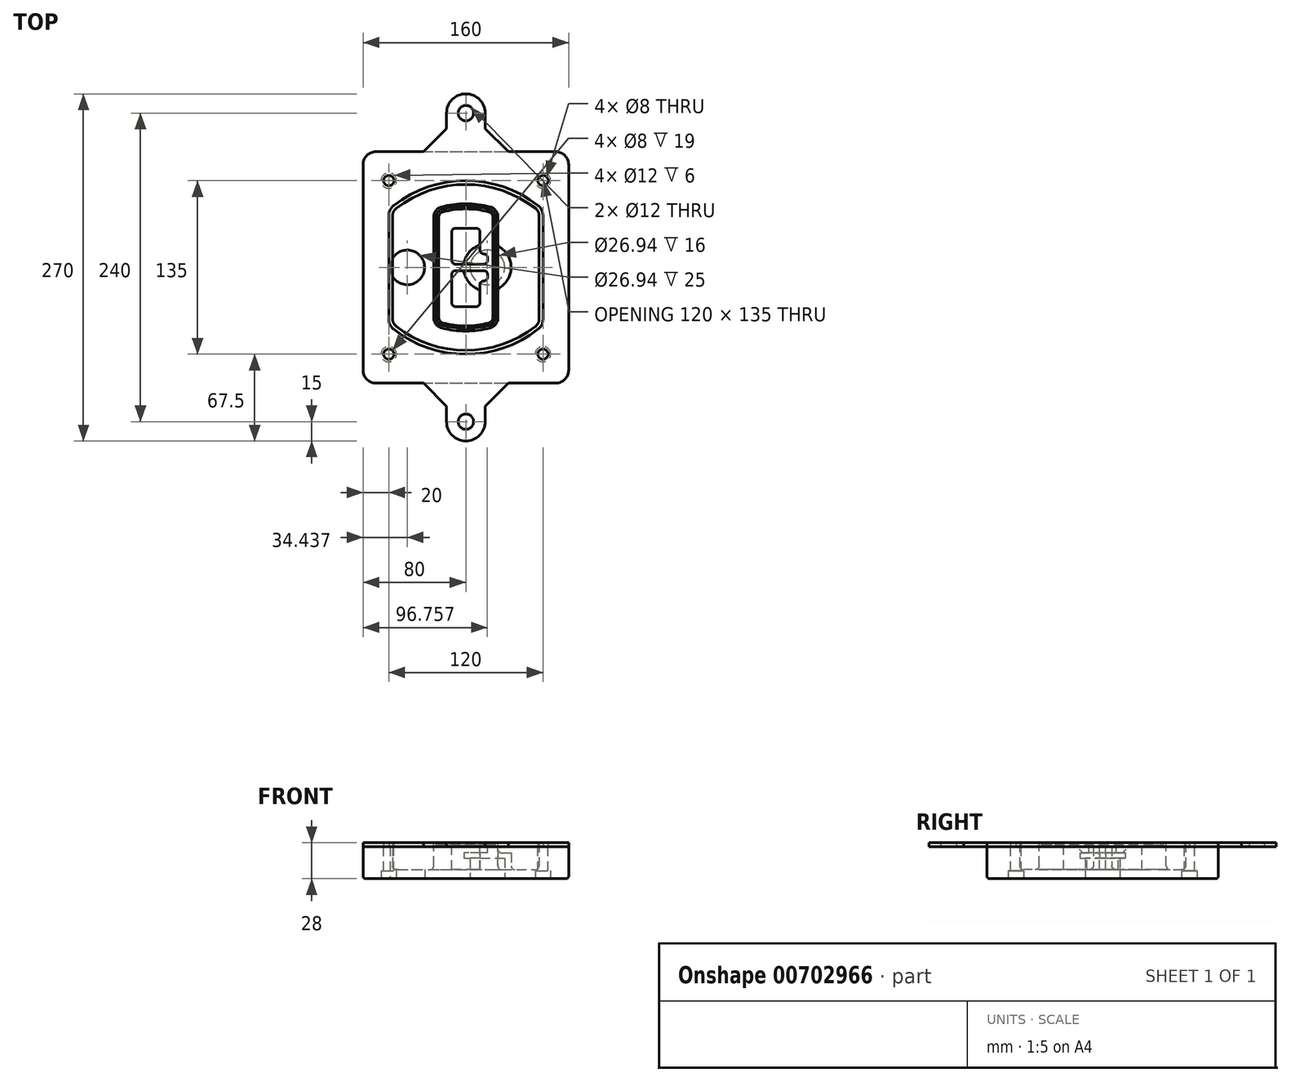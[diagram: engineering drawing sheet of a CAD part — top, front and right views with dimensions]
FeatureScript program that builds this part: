
annotation { "Feature Type Name" : "Feature", "Feature Type Description" : "" }
export const myFeature = defineFeature(function(context is Context, id is Id, definition is map)
    precondition{}
    {
        {
            var Q0;
            Q0=qCreatedBy(makeId("Top.planeOp"),FACE);
            var sketch = newSketch(context, id + "F0", { "sketchPlane" : qUnion([Q0])});
            skPoint(sketch, "E0.rect.middle", {"position": v(0, 0) * mm});
            skLineSegment(sketch, "E1.bottom", {"start": v(-70, -90) * mm, "end": v(70, -90) * mm});
            skLineSegment(sketch, "E1.top", {"start": v(-70, 90) * mm, "end": v(70, 90) * mm});
            skLineSegment(sketch, "E1.left", {"start": v(-80, -80) * mm, "end": v(-80, 80) * mm});
            skLineSegment(sketch, "E1.right", {"start": v(80, -80) * mm, "end": v(80, 80) * mm});
            skLineSegment(sketch, "E2", {"start": v(-80, 90) * mm, "end": v(80, -90) * mm, "construction": true});
            skLineSegment(sketch, "E3", {"start": v(80, 90) * mm, "end": v(-80, -90) * mm, "construction": true});
            skCircle(sketch, "E4", {"center": v(-60, 67.5) * mm, "radius": 4 * mm});
            skCircle(sketch, "E5", {"center": v(60, 67.5) * mm, "radius": 4 * mm});
            skCircle(sketch, "E6", {"center": v(60, -67.5) * mm, "radius": 4 * mm});
            skCircle(sketch, "E7", {"center": v(-60, -67.5) * mm, "radius": 4 * mm});
            skLineSegment(sketch, "E8", {"start": v(-60, 67.5) * mm, "end": v(60, 67.5) * mm, "construction": true});
            skLineSegment(sketch, "E9", {"start": v(60, 67.5) * mm, "end": v(60, -67.5) * mm, "construction": true});
            skLineSegment(sketch, "E10", {"start": v(60, -67.5) * mm, "end": v(-60, -67.5) * mm, "construction": true});
            skLineSegment(sketch, "E11", {"start": v(-60, -67.5) * mm, "end": v(-60, 67.5) * mm, "construction": true});
            skLineSegment(sketch, "E12", {"start": v(-60, 40.3) * mm, "end": v(-60, -40.3) * mm});
            skLineSegment(sketch, "E13", {"start": v(60, 40.3) * mm, "end": v(60, -40.3) * mm});
            skArc(sketch, "E14", {"start": v(56.15, 48.18) * mm, "mid": v(0, 67.5) * mm, "end": v(-56.15, 48.18) * mm});
            skArc(sketch, "E15", {"start": v(-56.15, -48.18) * mm, "mid": v(0, -67.5) * mm, "end": v(56.15, -48.18) * mm});
            skLineSegment(sketch, "E16", {"start": v(-60, 0) * mm, "end": v(60, 0) * mm, "construction": true});
            skPoint(sketch, "E17.visualSharp", {"position": v(-60, -45) * mm});
            skArc(sketch, "E17.filletArc", {"start": v(-60, -40.3) * mm, "mid": v(-58.99, -44.68) * mm, "end": v(-56.15, -48.18) * mm});
            skPoint(sketch, "E18.visualSharp", {"position": v(-60, 45) * mm});
            skArc(sketch, "E18.filletArc", {"start": v(-56.15, 48.18) * mm, "mid": v(-58.99, 44.68) * mm, "end": v(-60, 40.3) * mm});
            skPoint(sketch, "E19.visualSharp", {"position": v(60, 45) * mm});
            skArc(sketch, "E19.filletArc", {"start": v(60, 40.3) * mm, "mid": v(58.99, 44.68) * mm, "end": v(56.15, 48.18) * mm});
            skPoint(sketch, "E20.visualSharp", {"position": v(60, -45) * mm});
            skArc(sketch, "E20.filletArc", {"start": v(56.15, -48.18) * mm, "mid": v(58.99, -44.68) * mm, "end": v(60, -40.3) * mm});
            skPoint(sketch, "E21.visualSharp", {"position": v(-80, 90) * mm});
            skArc(sketch, "E21.filletArc", {"start": v(-70, 90) * mm, "mid": v(-77.07, 87.07) * mm, "end": v(-80, 80) * mm});
            skPoint(sketch, "E22.visualSharp", {"position": v(80, 90) * mm});
            skArc(sketch, "E22.filletArc", {"start": v(80, 80) * mm, "mid": v(77.07, 87.07) * mm, "end": v(70, 90) * mm});
            skPoint(sketch, "E23.visualSharp", {"position": v(80, -90) * mm});
            skArc(sketch, "E23.filletArc", {"start": v(70, -90) * mm, "mid": v(77.07, -87.07) * mm, "end": v(80, -80) * mm});
            skPoint(sketch, "E24.visualSharp", {"position": v(-80, -90) * mm});
            skArc(sketch, "E24.filletArc", {"start": v(-80, -80) * mm, "mid": v(-77.07, -87.07) * mm, "end": v(-70, -90) * mm});
            skArc(sketch, "E25.0", {"start": v(57, 40.3) * mm, "mid": v(56.3, 43.36) * mm, "end": v(54.3, 45.81) * mm});
            skLineSegment(sketch, "E25.1", {"start": v(57, 40.3) * mm, "end": v(57, -40.3) * mm});
            skArc(sketch, "E25.2", {"start": v(54.3, -45.81) * mm, "mid": v(56.3, -43.36) * mm, "end": v(57, -40.3) * mm});
            skArc(sketch, "E25.3", {"start": v(-54.3, -45.81) * mm, "mid": v(0, -64.5) * mm, "end": v(54.3, -45.81) * mm});
            skArc(sketch, "E25.4", {"start": v(-57, -40.3) * mm, "mid": v(-56.3, -43.36) * mm, "end": v(-54.3, -45.81) * mm});
            skArc(sketch, "E25.5", {"start": v(54.3, 45.81) * mm, "mid": v(0, 64.5) * mm, "end": v(-54.3, 45.81) * mm});
            skLineSegment(sketch, "E25.6", {"start": v(-57, 40.3) * mm, "end": v(-57, -40.3) * mm});
            skArc(sketch, "E25.7", {"start": v(-54.3, 45.81) * mm, "mid": v(-56.3, 43.36) * mm, "end": v(-57, 40.3) * mm});
            skArc(sketch, "E26.0", {"start": v(-58.62, 51.33) * mm, "mid": v(-62.58, 46.43) * mm, "end": v(-64, 40.3) * mm});
            skArc(sketch, "E26.1", {"start": v(58.62, 51.33) * mm, "mid": v(0, 71.5) * mm, "end": v(-58.62, 51.33) * mm});
            skArc(sketch, "E26.2", {"start": v(64, 40.3) * mm, "mid": v(62.58, 46.43) * mm, "end": v(58.62, 51.33) * mm});
            skLineSegment(sketch, "E26.3", {"start": v(64, 40.3) * mm, "end": v(64, -40.3) * mm});
            skArc(sketch, "E26.4", {"start": v(58.62, -51.33) * mm, "mid": v(62.58, -46.43) * mm, "end": v(64, -40.3) * mm});
            skLineSegment(sketch, "E26.5", {"start": v(-64, 40.3) * mm, "end": v(-64, -40.3) * mm});
            skArc(sketch, "E26.6", {"start": v(-58.62, -51.33) * mm, "mid": v(0, -71.5) * mm, "end": v(58.62, -51.33) * mm});
            skArc(sketch, "E26.7", {"start": v(-64, -40.3) * mm, "mid": v(-62.58, -46.43) * mm, "end": v(-58.62, -51.33) * mm});
            skSolve(sketch);
        }
        {
            var Q0;
            Q0=makeQuery(id+"F0.imprint","IMPRINT",FACE,{"disambiguationData":[TD([[makeQuery(id+"F0.imprint","IMPRINT",EDGE,{"derivedFrom":sQuery(id+"F0.wireOp",EDGE,"E1.bottom")}),1.0]])]});
            var Q1;
            Q1=makeQuery(id+"F0.imprint","IMPRINT",FACE,{"disambiguationData":[TD([[makeQuery(id+"F0.imprint","IMPRINT",EDGE,{"derivedFrom":sQuery(id+"F0.wireOp",EDGE,"E12")}),1.0]])]});
            var Q2;
            Q2=makeQuery(id+"F0.imprint","IMPRINT",FACE,{"disambiguationData":[TD([[makeQuery(id+"F0.imprint","IMPRINT",EDGE,{"derivedFrom":sQuery(id+"F0.wireOp",EDGE,"E25.0")}),1.0]])]});
            var Q3;
            Q3=makeQuery(id+"F0.imprint","IMPRINT",FACE,{"disambiguationData":[TD([[makeQuery(id+"F0.imprint","IMPRINT",EDGE,{"derivedFrom":sQuery(id+"F0.wireOp",EDGE,"E12")}),-1.0]])]});
            extrude(context, id + "F1", {"entities" : qUnion([Q0, Q1, Q2, Q3]), "oppositeDirection" : true, "depth" : 25 * mm});
        }
        {
            var Q0;
            Q0=makeQuery(id+"F0.imprint","IMPRINT",FACE,{"disambiguationData":[TD([[makeQuery(id+"F0.imprint","IMPRINT",EDGE,{"derivedFrom":sQuery(id+"F0.wireOp",EDGE,"E12")}),1.0]])]});
            extrude(context, id + "F2", {"entities" : qUnion([Q0]), "operationType" : NewBodyOperationType.ADD, "depth" : 3 * mm});
        }
        {
            var Q0;
            Q0=makeQuery(id+"F0.imprint","IMPRINT",FACE,{"disambiguationData":[TD([[makeQuery(id+"F0.imprint","IMPRINT",EDGE,{"derivedFrom":sQuery(id+"F0.wireOp",EDGE,"E25.0")}),1.0]])]});
            extrude(context, id + "F3", {"entities" : qUnion([Q0]), "operationType" : NewBodyOperationType.REMOVE, "oppositeDirection" : true, "depth" : 18 * mm});
        }
        {
            var Q0;
            Q0=makeQuery(id+"F2.opExtrude","CAP_FACE",FACE,{"disambiguationData":[OSD([sQuery(id+"F0.wireOp",EDGE,"E12"),sQuery(id+"F0.wireOp",EDGE,"E13"),sQuery(id+"F0.wireOp",EDGE,"E14"),sQuery(id+"F0.wireOp",EDGE,"E15"),sQuery(id+"F0.wireOp",EDGE,"E17.filletArc"),sQuery(id+"F0.wireOp",EDGE,"E18.filletArc"),sQuery(id+"F0.wireOp",EDGE,"E19.filletArc"),sQuery(id+"F0.wireOp",EDGE,"E20.filletArc"),sQuery(id+"F0.wireOp",EDGE,"E25.0"),sQuery(id+"F0.wireOp",EDGE,"E25.1"),sQuery(id+"F0.wireOp",EDGE,"E25.2"),sQuery(id+"F0.wireOp",EDGE,"E25.3"),sQuery(id+"F0.wireOp",EDGE,"E25.4"),sQuery(id+"F0.wireOp",EDGE,"E25.5"),sQuery(id+"F0.wireOp",EDGE,"E25.6"),sQuery(id+"F0.wireOp",EDGE,"E25.7")])],"isStart":false});
            var sketch = newSketch(context, id + "F4", { "sketchPlane" : qUnion([Q0])});
            skArc(sketch, "E27.0", {"start": v(-19.08, -46.97) * mm, "mid": v(0, -49.5) * mm, "end": v(19.08, -46.97) * mm});
            skArc(sketch, "E28.0", {"start": v(19.08, 46.97) * mm, "mid": v(0, 49.5) * mm, "end": v(-19.08, 46.97) * mm});
            skLineSegment(sketch, "E29", {"start": v(-25, 39.25) * mm, "end": v(-25, -39.25) * mm});
            skLineSegment(sketch, "E30", {"start": v(25, 39.25) * mm, "end": v(25, -39.25) * mm});
            skLineSegment(sketch, "E31", {"start": v(-25, 45.1) * mm, "end": v(25, 45.1) * mm, "construction": true});
            skLineSegment(sketch, "E32", {"start": v(-25, -45.1) * mm, "end": v(25, -45.1) * mm, "construction": true});
            skPoint(sketch, "E33.visualSharp", {"position": v(-25, 45.1) * mm});
            skArc(sketch, "E33.filletArc", {"start": v(-19.08, 46.97) * mm, "mid": v(-23.35, 44.11) * mm, "end": v(-25, 39.25) * mm});
            skPoint(sketch, "E34.visualSharp", {"position": v(25, 45.1) * mm});
            skArc(sketch, "E34.filletArc", {"start": v(25, 39.25) * mm, "mid": v(23.35, 44.11) * mm, "end": v(19.08, 46.97) * mm});
            skPoint(sketch, "E35.visualSharp", {"position": v(25, -45.1) * mm});
            skArc(sketch, "E35.filletArc", {"start": v(19.08, -46.97) * mm, "mid": v(23.35, -44.11) * mm, "end": v(25, -39.25) * mm});
            skPoint(sketch, "E36.visualSharp", {"position": v(-25, -45.1) * mm});
            skArc(sketch, "E36.filletArc", {"start": v(-25, -39.25) * mm, "mid": v(-23.35, -44.11) * mm, "end": v(-19.08, -46.97) * mm});
            skArc(sketch, "E37.0", {"start": v(54.3, 45.81) * mm, "mid": v(0, 64.5) * mm, "end": v(-54.3, 45.81) * mm});
            skArc(sketch, "E37.1", {"start": v(-54.3, 45.81) * mm, "mid": v(-56.3, 43.36) * mm, "end": v(-57, 40.3) * mm});
            skLineSegment(sketch, "E37.2", {"start": v(-57, 40.3) * mm, "end": v(-57, -40.3) * mm});
            skArc(sketch, "E37.3", {"start": v(-57, -40.3) * mm, "mid": v(-56.3, -43.36) * mm, "end": v(-54.3, -45.81) * mm});
            skArc(sketch, "E37.4", {"start": v(-54.3, -45.81) * mm, "mid": v(0, -64.5) * mm, "end": v(54.3, -45.81) * mm});
            skArc(sketch, "E37.5", {"start": v(54.3, -45.81) * mm, "mid": v(56.3, -43.36) * mm, "end": v(57, -40.3) * mm});
            skLineSegment(sketch, "E37.6", {"start": v(57, 40.3) * mm, "end": v(57, -40.3) * mm});
            skArc(sketch, "E37.7", {"start": v(57, 40.3) * mm, "mid": v(56.3, 43.36) * mm, "end": v(54.3, 45.81) * mm});
            skLineSegment(sketch, "E38.0", {"start": v(23, 39.25) * mm, "end": v(23, -39.25) * mm});
            skArc(sketch, "E38.1", {"start": v(18.56, -45.04) * mm, "mid": v(21.76, -42.9) * mm, "end": v(23, -39.25) * mm});
            skArc(sketch, "E38.2", {"start": v(-18.56, -45.04) * mm, "mid": v(0, -47.5) * mm, "end": v(18.56, -45.04) * mm});
            skArc(sketch, "E38.3", {"start": v(-23, -39.25) * mm, "mid": v(-21.76, -42.9) * mm, "end": v(-18.56, -45.04) * mm});
            skLineSegment(sketch, "E38.4", {"start": v(-23, 39.25) * mm, "end": v(-23, -39.25) * mm});
            skArc(sketch, "E38.5", {"start": v(23, 39.25) * mm, "mid": v(21.76, 42.9) * mm, "end": v(18.56, 45.04) * mm});
            skArc(sketch, "E38.6", {"start": v(-18.56, 45.04) * mm, "mid": v(-21.76, 42.9) * mm, "end": v(-23, 39.25) * mm});
            skArc(sketch, "E38.7", {"start": v(18.56, 45.04) * mm, "mid": v(0, 47.5) * mm, "end": v(-18.56, 45.04) * mm});
            skArc(sketch, "E39.0", {"start": v(21, 39.25) * mm, "mid": v(20.18, 41.68) * mm, "end": v(18.04, 43.1) * mm});
            skLineSegment(sketch, "E39.1", {"start": v(21, 39.25) * mm, "end": v(21, -39.25) * mm});
            skArc(sketch, "E39.2", {"start": v(18.04, -43.1) * mm, "mid": v(20.18, -41.68) * mm, "end": v(21, -39.25) * mm});
            skArc(sketch, "E39.3", {"start": v(-18.04, -43.1) * mm, "mid": v(0, -45.5) * mm, "end": v(18.04, -43.1) * mm});
            skArc(sketch, "E39.4", {"start": v(-21, -39.25) * mm, "mid": v(-20.18, -41.68) * mm, "end": v(-18.04, -43.1) * mm});
            skArc(sketch, "E39.5", {"start": v(18.04, 43.1) * mm, "mid": v(0, 45.5) * mm, "end": v(-18.04, 43.1) * mm});
            skLineSegment(sketch, "E39.6", {"start": v(-21, 39.25) * mm, "end": v(-21, -39.25) * mm});
            skArc(sketch, "E39.7", {"start": v(-18.04, 43.1) * mm, "mid": v(-20.18, 41.68) * mm, "end": v(-21, 39.25) * mm});
            skLineSegment(sketch, "E40", {"start": v(-25, 0) * mm, "end": v(25, 0) * mm, "construction": true});
            skLineSegment(sketch, "E41", {"start": v(-11, 5.5) * mm, "end": v(-11, 27.5) * mm});
            skLineSegment(sketch, "E42", {"start": v(-8, 30.5) * mm, "end": v(8, 30.5) * mm});
            skLineSegment(sketch, "E43", {"start": v(11, 27.5) * mm, "end": v(11, 13.5) * mm});
            skLineSegment(sketch, "E44", {"start": v(14, 10.5) * mm, "end": v(14, 10.5) * mm});
            skLineSegment(sketch, "E45", {"start": v(17, 7.5) * mm, "end": v(17, 5.5) * mm});
            skLineSegment(sketch, "E46", {"start": v(14, 2.5) * mm, "end": v(-8, 2.5) * mm});
            skPoint(sketch, "E47.visualSharp", {"position": v(-11, 30.5) * mm});
            skArc(sketch, "E47.filletArc", {"start": v(-8, 30.5) * mm, "mid": v(-10.12, 29.62) * mm, "end": v(-11, 27.5) * mm});
            skPoint(sketch, "E48.visualSharp", {"position": v(11, 30.5) * mm});
            skArc(sketch, "E48.filletArc", {"start": v(11, 27.5) * mm, "mid": v(10.12, 29.62) * mm, "end": v(8, 30.5) * mm});
            skPoint(sketch, "E49.visualSharp", {"position": v(11, 10.5) * mm});
            skArc(sketch, "E49.filletArc", {"start": v(11, 13.5) * mm, "mid": v(11.88, 11.38) * mm, "end": v(14, 10.5) * mm});
            skPoint(sketch, "E50.visualSharp", {"position": v(17, 10.5) * mm});
            skArc(sketch, "E50.filletArc", {"start": v(17, 7.5) * mm, "mid": v(16.12, 9.62) * mm, "end": v(14, 10.5) * mm});
            skPoint(sketch, "E51.visualSharp", {"position": v(17, 2.5) * mm});
            skArc(sketch, "E51.filletArc", {"start": v(14, 2.5) * mm, "mid": v(16.12, 3.38) * mm, "end": v(17, 5.5) * mm});
            skPoint(sketch, "E52.visualSharp", {"position": v(-11, 2.5) * mm});
            skArc(sketch, "E52.filletArc", {"start": v(-11, 5.5) * mm, "mid": v(-10.12, 3.38) * mm, "end": v(-8, 2.5) * mm});
            skLineSegment(sketch, "E53.0.MirrorCS", {"start": v(14, -2.5) * mm, "end": v(-8, -2.5) * mm});
            skArc(sketch, "E54.0.MirrorCS", {"start": v(-11, -5.5) * mm, "mid": v(-10.12, -3.38) * mm, "end": v(-8, -2.5) * mm});
            skLineSegment(sketch, "E55.0.MirrorCS", {"start": v(-11, -5.5) * mm, "end": v(-11, -27.5) * mm});
            skArc(sketch, "E56.0.MirrorCS", {"start": v(-8, -30.5) * mm, "mid": v(-10.12, -29.62) * mm, "end": v(-11, -27.5) * mm});
            skLineSegment(sketch, "E57.0.MirrorCS", {"start": v(-8, -30.5) * mm, "end": v(8, -30.5) * mm});
            skArc(sketch, "E58.0.MirrorCS", {"start": v(11, -27.5) * mm, "mid": v(10.12, -29.62) * mm, "end": v(8, -30.5) * mm});
            skLineSegment(sketch, "E59.0.MirrorCS", {"start": v(11, -27.5) * mm, "end": v(11, -13.5) * mm});
            skArc(sketch, "E60.0.MirrorCS", {"start": v(11, -13.5) * mm, "mid": v(11.88, -11.38) * mm, "end": v(14, -10.5) * mm});
            skArc(sketch, "E61.0.MirrorCS", {"start": v(17, -7.5) * mm, "mid": v(16.12, -9.62) * mm, "end": v(14, -10.5) * mm});
            skLineSegment(sketch, "E62.0.MirrorCS", {"start": v(17, -7.5) * mm, "end": v(17, -5.5) * mm});
            skArc(sketch, "E63.0.MirrorCS", {"start": v(14, -2.5) * mm, "mid": v(16.12, -3.38) * mm, "end": v(17, -5.5) * mm});
            skSolve(sketch);
        }
        {
            var Q0;
            Q0=makeQuery(id+"F4.imprint","IMPRINT",FACE,{"disambiguationData":[TD([[makeQuery(id+"F4.imprint","IMPRINT",EDGE,{"derivedFrom":sQuery(id+"F4.wireOp",EDGE,"E27.0")}),1.0]])]});
            var Q1;
            Q1=makeQuery(id+"F4.imprint","IMPRINT",FACE,{"disambiguationData":[TD([[makeQuery(id+"F4.imprint","IMPRINT",EDGE,{"derivedFrom":sQuery(id+"F4.wireOp",EDGE,"E38.0")}),-1.0]])]});
            var Q2;
            Q2=makeQuery(id+"F4.imprint","IMPRINT",FACE,{"disambiguationData":[TD([[makeQuery(id+"F4.imprint","IMPRINT",EDGE,{"derivedFrom":sQuery(id+"F4.wireOp",EDGE,"E39.0")}),1.0]])]});
            extrude(context, id + "F5", {"entities" : qUnion([Q0, Q1, Q2]), "operationType" : NewBodyOperationType.ADD, "endBound" : BoundingType.UP_TO_NEXT, "oppositeDirection" : true, "depth" : 25 * mm});
        }
        {
            var Q0;
            Q0=makeQuery(id+"F4.imprint","IMPRINT",FACE,{"disambiguationData":[TD([[makeQuery(id+"F4.imprint","IMPRINT",EDGE,{"derivedFrom":sQuery(id+"F4.wireOp",EDGE,"E38.0")}),-1.0]])]});
            extrude(context, id + "F6", {"entities" : qUnion([Q0]), "operationType" : NewBodyOperationType.REMOVE, "oppositeDirection" : true, "depth" : 2 * mm});
        }
        {
            var Q0;
            Q0=makeQuery(id+"F1.opExtrude","CAP_FACE",FACE,{"disambiguationData":[OSD([sQuery(id+"F0.wireOp",EDGE,"E1.bottom"),sQuery(id+"F0.wireOp",EDGE,"E1.top"),sQuery(id+"F0.wireOp",EDGE,"E1.left"),sQuery(id+"F0.wireOp",EDGE,"E1.right"),sQuery(id+"F0.wireOp",EDGE,"E4"),sQuery(id+"F0.wireOp",EDGE,"E5"),sQuery(id+"F0.wireOp",EDGE,"E6"),sQuery(id+"F0.wireOp",EDGE,"E7"),sQuery(id+"F0.wireOp",EDGE,"E21.filletArc"),sQuery(id+"F0.wireOp",EDGE,"E22.filletArc"),sQuery(id+"F0.wireOp",EDGE,"E23.filletArc"),sQuery(id+"F0.wireOp",EDGE,"E24.filletArc")])],"isStart":false});
            var sketch = newSketch(context, id + "F7", { "sketchPlane" : qUnion([Q0])});
            skCircle(sketch, "E64", {"center": v(16.76, 0) * mm, "radius": 13.47 * mm});
            skCircle(sketch, "E65", {"center": v(-45.56, 0) * mm, "radius": 13.47 * mm});
            skLineSegment(sketch, "E66", {"start": v(80, 0) * mm, "end": v(-80, 0) * mm});
            skCircle(sketch, "E67", {"center": v(16.76, 0) * mm, "radius": 18.47 * mm});
            skCircle(sketch, "E68", {"center": v(60, -67.5) * mm, "radius": 6 * mm});
            skCircle(sketch, "E69", {"center": v(-60, -67.5) * mm, "radius": 6 * mm});
            skCircle(sketch, "E70", {"center": v(-60, 67.5) * mm, "radius": 6 * mm});
            skCircle(sketch, "E71", {"center": v(60, 67.5) * mm, "radius": 6 * mm});
            skSolve(sketch);
        }
        {
            var Q0;
            {var subQ1=sQuery(id+"F7.wireOp",EDGE,"E66");var subQ4=sQuery(id+"F7.wireOp",EDGE,"E64");var subQ6=makeQuery(id+"F7.imprint","INTERSECT",VERTEX,{"disambiguationData":[OD(0.0)],"derivedFrom":[subQ4,subQ1]});Q0=makeQuery(id+"F7.imprint","IMPRINT",FACE,{"disambiguationData":[TD([[makeQuery(id+"F7.imprint","IMPRINT",EDGE,{"disambiguationData":[TD([[subQ6,-1.0]])],"derivedFrom":subQ4}),-1.0]])]});}
            var Q1;
            {var subQ0=sQuery(id+"F7.wireOp",EDGE,"E66");var subQ1=sQuery(id+"F7.wireOp",EDGE,"E64");var subQ3=makeQuery(id+"F7.imprint","INTERSECT",VERTEX,{"disambiguationData":[OD(0.0)],"derivedFrom":[subQ1,subQ0]});Q1=makeQuery(id+"F7.imprint","IMPRINT",FACE,{"disambiguationData":[TD([[makeQuery(id+"F7.imprint","IMPRINT",EDGE,{"disambiguationData":[TD([[subQ3,-1.0]])],"derivedFrom":subQ1}),1.0]])]});}
            var Q2;
            {var subQ0=sQuery(id+"F7.wireOp",EDGE,"E66");var subQ1=sQuery(id+"F7.wireOp",EDGE,"E64");var subQ3=makeQuery(id+"F7.imprint","INTERSECT",VERTEX,{"disambiguationData":[OD(0.0)],"derivedFrom":[subQ1,subQ0]});Q2=makeQuery(id+"F7.imprint","IMPRINT",FACE,{"disambiguationData":[TD([[makeQuery(id+"F7.imprint","IMPRINT",EDGE,{"disambiguationData":[TD([[subQ3,1.0]])],"derivedFrom":subQ1}),1.0]])]});}
            var Q3;
            {var subQ1=sQuery(id+"F7.wireOp",EDGE,"E66");var subQ4=sQuery(id+"F7.wireOp",EDGE,"E64");var subQ6=makeQuery(id+"F7.imprint","INTERSECT",VERTEX,{"disambiguationData":[OD(0.0)],"derivedFrom":[subQ4,subQ1]});Q3=makeQuery(id+"F7.imprint","IMPRINT",FACE,{"disambiguationData":[TD([[makeQuery(id+"F7.imprint","IMPRINT",EDGE,{"disambiguationData":[TD([[subQ6,1.0]])],"derivedFrom":subQ4}),-1.0]])]});}
            extrude(context, id + "F8", {"entities" : qUnion([Q0, Q1, Q2, Q3]), "operationType" : NewBodyOperationType.ADD, "oppositeDirection" : true, "depth" : 20 * mm});
        }
        {
            var Q0;
            {var subQ0=sQuery(id+"F7.wireOp",EDGE,"E66");var subQ1=sQuery(id+"F7.wireOp",EDGE,"E64");var subQ3=makeQuery(id+"F7.imprint","INTERSECT",VERTEX,{"disambiguationData":[OD(0.0)],"derivedFrom":[subQ1,subQ0]});Q0=makeQuery(id+"F7.imprint","IMPRINT",FACE,{"disambiguationData":[TD([[makeQuery(id+"F7.imprint","IMPRINT",EDGE,{"disambiguationData":[TD([[subQ3,-1.0]])],"derivedFrom":subQ1}),1.0]])]});}
            var Q1;
            {var subQ0=sQuery(id+"F7.wireOp",EDGE,"E66");var subQ1=sQuery(id+"F7.wireOp",EDGE,"E64");var subQ3=makeQuery(id+"F7.imprint","INTERSECT",VERTEX,{"disambiguationData":[OD(0.0)],"derivedFrom":[subQ1,subQ0]});Q1=makeQuery(id+"F7.imprint","IMPRINT",FACE,{"disambiguationData":[TD([[makeQuery(id+"F7.imprint","IMPRINT",EDGE,{"disambiguationData":[TD([[subQ3,1.0]])],"derivedFrom":subQ1}),1.0]])]});}
            extrude(context, id + "F9", {"entities" : qUnion([Q0, Q1]), "operationType" : NewBodyOperationType.REMOVE, "oppositeDirection" : true, "depth" : 16 * mm});
        }
        {
            var Q0;
            {var subQ0=sQuery(id+"F7.wireOp",EDGE,"E66");var subQ1=sQuery(id+"F7.wireOp",EDGE,"E65");var subQ3=makeQuery(id+"F7.imprint","INTERSECT",VERTEX,{"disambiguationData":[OD(0.0)],"derivedFrom":[subQ1,subQ0]});Q0=makeQuery(id+"F7.imprint","IMPRINT",FACE,{"disambiguationData":[TD([[makeQuery(id+"F7.imprint","IMPRINT",EDGE,{"disambiguationData":[TD([[subQ3,-1.0]])],"derivedFrom":subQ1}),1.0]])]});}
            var Q1;
            {var subQ0=sQuery(id+"F7.wireOp",EDGE,"E66");var subQ1=sQuery(id+"F7.wireOp",EDGE,"E65");var subQ3=makeQuery(id+"F7.imprint","INTERSECT",VERTEX,{"disambiguationData":[OD(0.0)],"derivedFrom":[subQ1,subQ0]});Q1=makeQuery(id+"F7.imprint","IMPRINT",FACE,{"disambiguationData":[TD([[makeQuery(id+"F7.imprint","IMPRINT",EDGE,{"disambiguationData":[TD([[subQ3,1.0]])],"derivedFrom":subQ1}),1.0]])]});}
            extrude(context, id + "F10", {"entities" : qUnion([Q0, Q1]), "operationType" : NewBodyOperationType.REMOVE, "oppositeDirection" : true, "depth" : 25 * mm});
        }
        {
            var Q0;
            Q0=makeQuery(id+"F7.imprint","IMPRINT",FACE,{"disambiguationData":[TD([[makeQuery(id+"F7.imprint","IMPRINT",EDGE,{"derivedFrom":sQuery(id+"F7.wireOp",EDGE,"E68")}),1.0]])]});
            var Q1;
            Q1=makeQuery(id+"F7.imprint","IMPRINT",FACE,{"disambiguationData":[TD([[makeQuery(id+"F7.imprint","IMPRINT",EDGE,{"derivedFrom":makeQuery(id+"F1.opExtrude","CAP_EDGE",EDGE,{"disambiguationData":[OSD([sQuery(id+"F0.wireOp",EDGE,"E5")])],"isStart":false})}),-1.0]])]});
            var Q2;
            Q2=makeQuery(id+"F7.imprint","IMPRINT",FACE,{"disambiguationData":[TD([[makeQuery(id+"F7.imprint","IMPRINT",EDGE,{"derivedFrom":sQuery(id+"F7.wireOp",EDGE,"E69")}),1.0]])]});
            var Q3;
            Q3=makeQuery(id+"F7.imprint","IMPRINT",FACE,{"disambiguationData":[TD([[makeQuery(id+"F7.imprint","IMPRINT",EDGE,{"derivedFrom":makeQuery(id+"F1.opExtrude","CAP_EDGE",EDGE,{"disambiguationData":[OSD([sQuery(id+"F0.wireOp",EDGE,"E4")])],"isStart":false})}),-1.0]])]});
            var Q4;
            Q4=makeQuery(id+"F7.imprint","IMPRINT",FACE,{"disambiguationData":[TD([[makeQuery(id+"F7.imprint","IMPRINT",EDGE,{"derivedFrom":sQuery(id+"F7.wireOp",EDGE,"E70")}),1.0]])]});
            var Q5;
            Q5=makeQuery(id+"F7.imprint","IMPRINT",FACE,{"disambiguationData":[TD([[makeQuery(id+"F7.imprint","IMPRINT",EDGE,{"derivedFrom":makeQuery(id+"F1.opExtrude","CAP_EDGE",EDGE,{"disambiguationData":[OSD([sQuery(id+"F0.wireOp",EDGE,"E7")])],"isStart":false})}),-1.0]])]});
            var Q6;
            Q6=makeQuery(id+"F7.imprint","IMPRINT",FACE,{"disambiguationData":[TD([[makeQuery(id+"F7.imprint","IMPRINT",EDGE,{"derivedFrom":sQuery(id+"F7.wireOp",EDGE,"E71")}),1.0]])]});
            var Q7;
            Q7=makeQuery(id+"F7.imprint","IMPRINT",FACE,{"disambiguationData":[TD([[makeQuery(id+"F7.imprint","IMPRINT",EDGE,{"derivedFrom":makeQuery(id+"F1.opExtrude","CAP_EDGE",EDGE,{"disambiguationData":[OSD([sQuery(id+"F0.wireOp",EDGE,"E6")])],"isStart":false})}),-1.0]])]});
            extrude(context, id + "F11", {"entities" : qUnion([Q0, Q1, Q2, Q3, Q4, Q5, Q6, Q7]), "operationType" : NewBodyOperationType.REMOVE, "oppositeDirection" : true, "depth" : 6 * mm});
        }
        {
            var Q0;
            Q0=makeQuery(id+"F9.boolean.opBoolean","COPY",FACE,{"derivedFrom":makeQuery(id+"F9.opExtrude","CAP_FACE",FACE,{"disambiguationData":[OSD([sQuery(id+"F7.wireOp",EDGE,"E64")])],"isStart":false})});
            var sketch = newSketch(context, id + "F12", { "sketchPlane" : qUnion([Q0])});
            skArc(sketch, "E72.0", {"start": v(11, 17.55) * mm, "mid": v(2.57, 11.82) * mm, "end": v(-1.54, 2.5) * mm});
            skArc(sketch, "E72.1", {"start": v(-1.54, -2.5) * mm, "mid": v(2.57, -11.82) * mm, "end": v(11, -17.55) * mm});
            skLineSegment(sketch, "E73", {"start": v(-1.54, -2.5) * mm, "end": v(14, -2.5) * mm});
            skLineSegment(sketch, "E74.0", {"start": v(14, 2.5) * mm, "end": v(-1.54, 2.5) * mm});
            skArc(sketch, "E74.1", {"start": v(14, 2.5) * mm, "mid": v(16.12, 3.38) * mm, "end": v(17, 5.5) * mm});
            skLineSegment(sketch, "E74.2", {"start": v(17, 7.5) * mm, "end": v(17, 5.5) * mm});
            skArc(sketch, "E74.3", {"start": v(17, 7.5) * mm, "mid": v(16.12, 9.62) * mm, "end": v(14, 10.5) * mm});
            skArc(sketch, "E74.4", {"start": v(11, 13.5) * mm, "mid": v(11.88, 11.38) * mm, "end": v(14, 10.5) * mm});
            skLineSegment(sketch, "E74.5", {"start": v(11, 17.55) * mm, "end": v(11, 13.5) * mm});
            skLineSegment(sketch, "E74.7", {"start": v(14, -2.5) * mm, "end": v(-1.54, -2.5) * mm});
            skArc(sketch, "E74.8", {"start": v(14, -2.5) * mm, "mid": v(16.12, -3.38) * mm, "end": v(17, -5.5) * mm});
            skLineSegment(sketch, "E74.9", {"start": v(17, -7.5) * mm, "end": v(17, -5.5) * mm});
            skArc(sketch, "E74.10", {"start": v(17, -7.5) * mm, "mid": v(16.12, -9.62) * mm, "end": v(14, -10.5) * mm});
            skArc(sketch, "E74.11", {"start": v(11, -13.5) * mm, "mid": v(11.88, -11.38) * mm, "end": v(14, -10.5) * mm});
            skLineSegment(sketch, "E74.12", {"start": v(11, -17.55) * mm, "end": v(11, -13.5) * mm});
            skPoint(sketch, "E75.orphan", {"position": v(11, -27.5) * mm});
            skPoint(sketch, "E76.orphan", {"position": v(-8, -2.5) * mm});
            skPoint(sketch, "E77.orphan", {"position": v(-8, 2.5) * mm});
            skPoint(sketch, "E78.orphan", {"position": v(11, 27.5) * mm});
            skSolve(sketch);
        }
        {
            var Q0;
            {var subQ7=sQuery(id+"F12.wireOp",EDGE,"E72.0");var subQ14=sQuery(id+"F12.wireOp",EDGE,"E72.1");var subQ16=sQuery(id+"F12.wireOp",EDGE,"E74.1");var subQ18=sQuery(id+"F12.wireOp",EDGE,"E74.8");Q0=qUnion([makeQuery(id+"F12.imprint","IMPRINT",FACE,{"disambiguationData":[TD([[makeQuery(id+"F12.imprint","IMPRINT",EDGE,{"derivedFrom":subQ7}),1.0]])]}),makeQuery(id+"F12.imprint","IMPRINT",FACE,{"disambiguationData":[TD([[makeQuery(id+"F12.imprint","IMPRINT",EDGE,{"derivedFrom":subQ14}),1.0]])]}),makeQuery(id+"F12.imprint","IMPRINT",FACE,{"disambiguationData":[TD([[makeQuery(id+"F12.imprint","IMPRINT",EDGE,{"derivedFrom":subQ16}),1.0]])]}),makeQuery(id+"F12.imprint","IMPRINT",FACE,{"disambiguationData":[TD([[makeQuery(id+"F12.imprint","IMPRINT",EDGE,{"derivedFrom":subQ18}),-1.0]])]})]);}
            var Q1;
            Q1=makeQuery(id+"F5.boolean.opBoolean","SPLIT",FACE,{"disambiguationData":[TD([makeQuery(id+"F5.opExtrude","SWEPT_FACE",FACE,{"disambiguationData":[OSD([sQuery(id+"F4.wireOp",EDGE,"E41")])]})])],"derivedFrom":makeQuery(id+"F3.boolean.opBoolean","COPY",FACE,{"derivedFrom":makeQuery(id+"F3.opExtrude","CAP_FACE",FACE,{"disambiguationData":[OSD([sQuery(id+"F0.wireOp",EDGE,"E25.0"),sQuery(id+"F0.wireOp",EDGE,"E25.1"),sQuery(id+"F0.wireOp",EDGE,"E25.2"),sQuery(id+"F0.wireOp",EDGE,"E25.3"),sQuery(id+"F0.wireOp",EDGE,"E25.4"),sQuery(id+"F0.wireOp",EDGE,"E25.5"),sQuery(id+"F0.wireOp",EDGE,"E25.6"),sQuery(id+"F0.wireOp",EDGE,"E25.7")])],"isStart":false})})});
            extrude(context, id + "F13", {"entities" : qUnion([Q0]), "operationType" : NewBodyOperationType.REMOVE, "endBound" : BoundingType.UP_TO_SURFACE, "endBoundEntityFace" : qUnion([Q1]), "depth" : 25 * mm});
        }
        {
            var Q0;
            Q0=makeQuery(id+"F3.boolean.opBoolean","COPY",EDGE,{"derivedFrom":makeQuery(id+"F3.opExtrude","CAP_EDGE",EDGE,{"disambiguationData":[OSD([sQuery(id+"F0.wireOp",EDGE,"E25.6")])],"isStart":false})});
            var Q1;
            Q1=makeQuery(id+"F8.boolean.opBoolean","INTERSECT",EDGE,{"derivedFrom":[makeQuery(id+"F5.opExtrude","SWEPT_FACE",FACE,{"disambiguationData":[OSD([sQuery(id+"F4.wireOp",EDGE,"E30")])]}),makeQuery(id+"F8.opExtrude","CAP_FACE",FACE,{"disambiguationData":[OSD([sQuery(id+"F7.wireOp",EDGE,"E67")])],"isStart":false})]});
            var Q2;
            Q2=makeQuery(id+"F8.boolean.opBoolean","INTERSECT",EDGE,{"disambiguationData":[OD(1.0)],"derivedFrom":[makeQuery(id+"F5.opExtrude","SWEPT_FACE",FACE,{"disambiguationData":[OSD([sQuery(id+"F4.wireOp",EDGE,"E30")])]}),makeQuery(id+"F8.opExtrude","SWEPT_FACE",FACE,{"disambiguationData":[OSD([sQuery(id+"F7.wireOp",EDGE,"E67")])]})]});
            var Q3;
            {var subQ0=sQuery(id+"F4.wireOp",EDGE,"E30");Q3=makeQuery(id+"F8.boolean.opBoolean","SPLIT",EDGE,{"disambiguationData":[TD([makeQuery(id+"F5.opExtrude","SWEPT_FACE",FACE,{"disambiguationData":[OSD([sQuery(id+"F4.wireOp",EDGE,"E35.filletArc")])]})])],"derivedFrom":makeQuery(id+"F5.opExtrude","CAP_EDGE",EDGE,{"disambiguationData":[OSD([subQ0])],"isStart":false})});}
            var Q4;
            {var subQ0=sQuery(id+"F0.wireOp",EDGE,"E25.7");var subQ1=sQuery(id+"F0.wireOp",EDGE,"E25.1");var subQ2=sQuery(id+"F0.wireOp",EDGE,"E25.6");var subQ3=sQuery(id+"F0.wireOp",EDGE,"E25.5");var subQ4=sQuery(id+"F0.wireOp",EDGE,"E25.4");var subQ5=sQuery(id+"F0.wireOp",EDGE,"E25.0");var subQ6=sQuery(id+"F0.wireOp",EDGE,"E25.2");var subQ7=sQuery(id+"F0.wireOp",EDGE,"E25.3");Q4=makeQuery(id+"F8.boolean.opBoolean","INTERSECT",EDGE,{"derivedFrom":[makeQuery(id+"F5.boolean.opBoolean","SPLIT",FACE,{"disambiguationData":[TD([makeQuery(id+"F2.opExtrude","SWEPT_FACE",FACE,{"disambiguationData":[OSD([subQ5])]})])],"derivedFrom":makeQuery(id+"F3.boolean.opBoolean","COPY",FACE,{"derivedFrom":makeQuery(id+"F3.opExtrude","CAP_FACE",FACE,{"disambiguationData":[OSD([subQ5,subQ1,subQ6,subQ7,subQ4,subQ3,subQ2,subQ0])],"isStart":false})})}),makeQuery(id+"F8.opExtrude","SWEPT_FACE",FACE,{"disambiguationData":[OSD([sQuery(id+"F7.wireOp",EDGE,"E67")])]})]});}
            var Q5;
            Q5=makeQuery(id+"F8.boolean.opBoolean","INTERSECT",EDGE,{"disambiguationData":[OD(0.0)],"derivedFrom":[makeQuery(id+"F5.opExtrude","SWEPT_FACE",FACE,{"disambiguationData":[OSD([sQuery(id+"F4.wireOp",EDGE,"E30")])]}),makeQuery(id+"F8.opExtrude","SWEPT_FACE",FACE,{"disambiguationData":[OSD([sQuery(id+"F7.wireOp",EDGE,"E67")])]})]});
            fillet(context, id + "F14", {"entities" : qUnion([Q0, Q1, Q2, Q3, Q4, Q5]), "radius" : 3 * mm, "tangentPropagation" : true, "allowEdgeOverflow" : false});
        }
        {
            var Q0;
            Q0=makeQuery(id+"F1.opExtrude","CAP_EDGE",EDGE,{"disambiguationData":[OSD([sQuery(id+"F0.wireOp",EDGE,"E1.bottom")])],"isStart":false});
            fillet(context, id + "F15", {"entities" : qUnion([Q0]), "radius" : 2 * mm, "tangentPropagation" : true, "allowEdgeOverflow" : false});
        }
        {
            var Q0;
            {var subQ0=sQuery(id+"F0.wireOp",EDGE,"E21.filletArc");var subQ1=sQuery(id+"F0.wireOp",EDGE,"E7");var subQ2=sQuery(id+"F0.wireOp",EDGE,"E6");var subQ3=sQuery(id+"F0.wireOp",EDGE,"E5");var subQ4=sQuery(id+"F0.wireOp",EDGE,"E4");var subQ5=sQuery(id+"F0.wireOp",EDGE,"E22.filletArc");var subQ6=sQuery(id+"F0.wireOp",EDGE,"E1.bottom");var subQ7=sQuery(id+"F0.wireOp",EDGE,"E1.right");var subQ8=sQuery(id+"F0.wireOp",EDGE,"E1.top");var subQ9=sQuery(id+"F0.wireOp",EDGE,"E1.left");var subQ10=sQuery(id+"F0.wireOp",EDGE,"E23.filletArc");var subQ11=sQuery(id+"F0.wireOp",EDGE,"E24.filletArc");Q0=makeQuery(id+"F2.boolean.opBoolean","SPLIT",FACE,{"disambiguationData":[TD([makeQuery(id+"F1.opExtrude","SWEPT_FACE",FACE,{"disambiguationData":[OSD([subQ6])]})])],"derivedFrom":makeQuery(id+"F1.opExtrude","CAP_FACE",FACE,{"disambiguationData":[OSD([subQ6,subQ8,subQ9,subQ7,subQ4,subQ3,subQ2,subQ1,subQ0,subQ5,subQ10,subQ11])],"isStart":true})});}
            var sketch = newSketch(context, id + "F16", { "sketchPlane" : qUnion([Q0])});
            skLineSegment(sketch, "E79", {"start": v(0, 90) * mm, "end": v(0, 120) * mm, "construction": true});
            skLineSegment(sketch, "E80", {"start": v(-33, 90) * mm, "end": v(-15, 108) * mm});
            skLineSegment(sketch, "E81", {"start": v(-15, 108) * mm, "end": v(-15, 120) * mm});
            skLineSegment(sketch, "E82", {"start": v(33, 90) * mm, "end": v(15, 108) * mm});
            skLineSegment(sketch, "E83", {"start": v(15, 108) * mm, "end": v(15, 120) * mm});
            skCircle(sketch, "E84", {"center": v(0, 120) * mm, "radius": 6 * mm});
            skArc(sketch, "E85", {"start": v(15, 120) * mm, "mid": v(0, 135) * mm, "end": v(-15, 120) * mm});
            skLineSegment(sketch, "E86", {"start": v(-80, 0) * mm, "end": v(80, 0) * mm, "construction": true});
            skLineSegment(sketch, "E87.MirrorCS", {"start": v(-33, -90) * mm, "end": v(-15, -108) * mm});
            skLineSegment(sketch, "E88.MirrorCS", {"start": v(-15, -108) * mm, "end": v(-15, -120) * mm});
            skArc(sketch, "E89.MirrorCS", {"start": v(15, -120) * mm, "mid": v(0, -135) * mm, "end": v(-15, -120) * mm});
            skCircle(sketch, "E90.MirrorC", {"center": v(0, -120) * mm, "radius": 6 * mm});
            skLineSegment(sketch, "E91.MirrorCS", {"start": v(15, -108) * mm, "end": v(15, -120) * mm});
            skLineSegment(sketch, "E92.MirrorCS", {"start": v(33, -90) * mm, "end": v(15, -108) * mm});
            skSolve(sketch);
        }
        {
            var Q0;
            {var subQ0=sQuery(id+"F16.wireOp",EDGE,"E87.MirrorCS");Q0=makeQuery(id+"F16.imprint","IMPRINT",FACE,{"disambiguationData":[TD([[makeQuery(id+"F16.imprint","IMPRINT",EDGE,{"derivedFrom":subQ0}),1.0]])]});}
            var Q1;
            {var subQ1=sQuery(id+"F16.wireOp",EDGE,"E80");Q1=makeQuery(id+"F16.imprint","IMPRINT",FACE,{"disambiguationData":[TD([[makeQuery(id+"F16.imprint","IMPRINT",EDGE,{"derivedFrom":subQ1}),-1.0]])]});}
            var Q2;
            Q2=makeQuery(id+"F16.imprint","IMPRINT",FACE,{"disambiguationData":[TD([[makeQuery(id+"F16.imprint","IMPRINT",EDGE,{"derivedFrom":makeQuery(id+"F1.opExtrude","CAP_EDGE",EDGE,{"disambiguationData":[OSD([sQuery(id+"F0.wireOp",EDGE,"E1.left")])],"isStart":true})}),-1.0]])]});
            var Q3;
            Q3=makeQuery(id+"F2.opExtrude","CAP_FACE",FACE,{"disambiguationData":[OSD([sQuery(id+"F0.wireOp",EDGE,"E12"),sQuery(id+"F0.wireOp",EDGE,"E13"),sQuery(id+"F0.wireOp",EDGE,"E14"),sQuery(id+"F0.wireOp",EDGE,"E15"),sQuery(id+"F0.wireOp",EDGE,"E17.filletArc"),sQuery(id+"F0.wireOp",EDGE,"E18.filletArc"),sQuery(id+"F0.wireOp",EDGE,"E19.filletArc"),sQuery(id+"F0.wireOp",EDGE,"E20.filletArc"),sQuery(id+"F0.wireOp",EDGE,"E25.0"),sQuery(id+"F0.wireOp",EDGE,"E25.1"),sQuery(id+"F0.wireOp",EDGE,"E25.2"),sQuery(id+"F0.wireOp",EDGE,"E25.3"),sQuery(id+"F0.wireOp",EDGE,"E25.4"),sQuery(id+"F0.wireOp",EDGE,"E25.5"),sQuery(id+"F0.wireOp",EDGE,"E25.6"),sQuery(id+"F0.wireOp",EDGE,"E25.7")])],"isStart":false});
            extrude(context, id + "F17", {"entities" : qUnion([Q0, Q1, Q2]), "endBound" : BoundingType.UP_TO_SURFACE, "depth" : 25 * mm, "endBoundEntityFace" : qUnion([Q3]), "offsetDistance" : 25 * mm});
        }
    });
